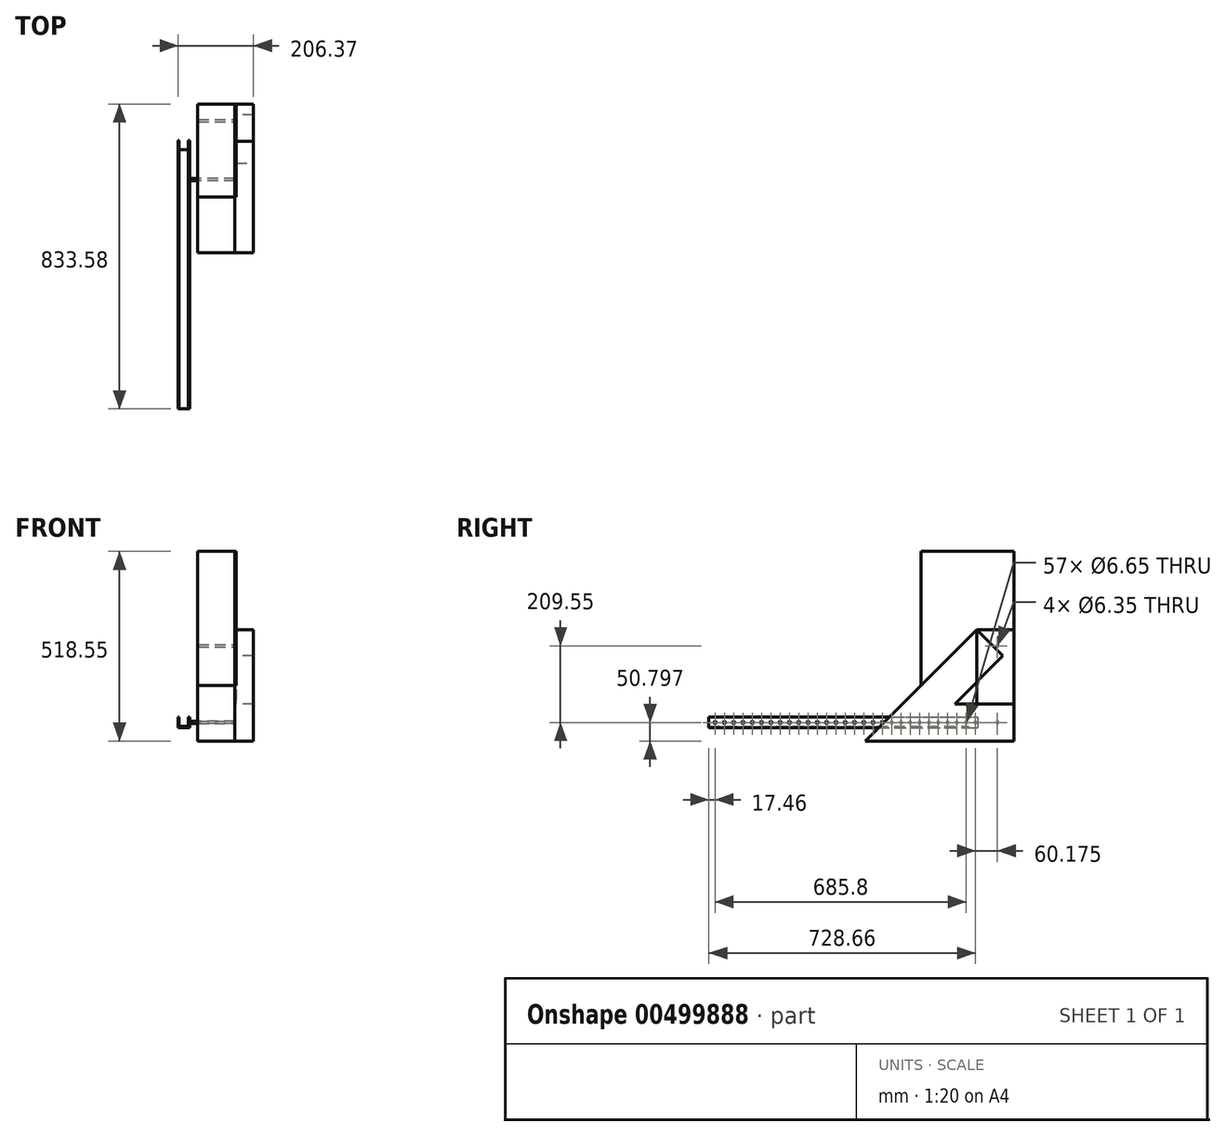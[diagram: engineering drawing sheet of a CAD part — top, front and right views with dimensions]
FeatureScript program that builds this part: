
annotation { "Feature Type Name" : "Feature", "Feature Type Description" : "" }
export const myFeature = defineFeature(function(context is Context, id is Id, definition is map)
    precondition{}
    {
        {
            var Q0;
            Q0=qCreatedBy(makeId("Front.planeOp"),FACE);
            var sketch = newSketch(context, id + "F0", { "sketchPlane" : qUnion([Q0])});
            skLineSegment(sketch, "E0", {"start": v(-56.5, 60.32) * mm, "end": v(-56.5, 31.75) * mm});
            skLineSegment(sketch, "E1", {"start": v(-56.5, 31.75) * mm, "end": v(-24.75, 31.75) * mm});
            skLineSegment(sketch, "E2", {"start": v(-24.75, 31.75) * mm, "end": v(-24.75, 60.33) * mm});
            skLineSegment(sketch, "E3", {"start": v(-24.75, 60.33) * mm, "end": v(-27.93, 60.33) * mm});
            skLineSegment(sketch, "E4", {"start": v(-27.93, 60.33) * mm, "end": v(-27.93, 34.92) * mm});
            skLineSegment(sketch, "E5", {"start": v(-27.93, 34.92) * mm, "end": v(-53.33, 34.92) * mm});
            skLineSegment(sketch, "E6", {"start": v(-53.33, 34.92) * mm, "end": v(-53.33, 60.32) * mm});
            skLineSegment(sketch, "E7", {"start": v(-53.33, 60.32) * mm, "end": v(-56.5, 60.32) * mm});
            skSolve(sketch);
        }
        {
            var Q0;
            Q0=qSketchRegion(id+"F0",true);
            extrude(context, id + "F1", {"entities" : qUnion([Q0]), "depth" : 735 * mm});
        }
        {
            var Q0;
            Q0=makeQuery(id+"F1.opExtrude","SWEPT_FACE",FACE,{"disambiguationData":[OSD([sQuery(id+"F0.wireOp",EDGE,"E2")])]});
            var sketch = newSketch(context, id + "F2", { "sketchPlane" : qUnion([Q0])});
            skLineSegment(sketch, "E8", {"start": v(-735.01, 46.04) * mm, "end": v(0, 46.04) * mm, "construction": true});
            skCircle(sketch, "E9", {"center": v(-6.35, 46.04) * mm, "radius": 3.18 * mm});
            skCircle(sketch, "E10", {"center": v(-31.75, 46.04) * mm, "radius": 3.32 * mm});
            skCircle(sketch, "E11.1.0.0", {"center": v(-57.15, 46.04) * mm, "radius": 3.32 * mm});
            skCircle(sketch, "E11.2.0.0", {"center": v(-82.55, 46.04) * mm, "radius": 3.32 * mm});
            skCircle(sketch, "E11.3.0.0", {"center": v(-107.95, 46.04) * mm, "radius": 3.32 * mm});
            skCircle(sketch, "E11.4.0.0", {"center": v(-133.35, 46.04) * mm, "radius": 3.32 * mm});
            skCircle(sketch, "E11.5.0.0", {"center": v(-158.75, 46.04) * mm, "radius": 3.32 * mm});
            skCircle(sketch, "E11.6.0.0", {"center": v(-184.15, 46.04) * mm, "radius": 3.32 * mm});
            skCircle(sketch, "E11.7.0.0", {"center": v(-209.55, 46.04) * mm, "radius": 3.32 * mm});
            skCircle(sketch, "E11.8.0.0", {"center": v(-234.95, 46.04) * mm, "radius": 3.32 * mm});
            skCircle(sketch, "E11.9.0.0", {"center": v(-260.35, 46.04) * mm, "radius": 3.32 * mm});
            skCircle(sketch, "E11.10.0.0", {"center": v(-285.75, 46.04) * mm, "radius": 3.32 * mm});
            skCircle(sketch, "E11.11.0.0", {"center": v(-311.15, 46.04) * mm, "radius": 3.32 * mm});
            skCircle(sketch, "E11.12.0.0", {"center": v(-336.55, 46.04) * mm, "radius": 3.32 * mm});
            skCircle(sketch, "E11.13.0.0", {"center": v(-361.95, 46.04) * mm, "radius": 3.32 * mm});
            skCircle(sketch, "E11.14.0.0", {"center": v(-387.35, 46.04) * mm, "radius": 3.32 * mm});
            skCircle(sketch, "E11.15.0.0", {"center": v(-412.75, 46.04) * mm, "radius": 3.32 * mm});
            skCircle(sketch, "E11.16.0.0", {"center": v(-438.15, 46.04) * mm, "radius": 3.32 * mm});
            skCircle(sketch, "E11.17.0.0", {"center": v(-463.55, 46.04) * mm, "radius": 3.32 * mm});
            skCircle(sketch, "E11.18.0.0", {"center": v(-488.95, 46.04) * mm, "radius": 3.32 * mm});
            skCircle(sketch, "E11.19.0.0", {"center": v(-514.35, 46.04) * mm, "radius": 3.32 * mm});
            skCircle(sketch, "E11.20.0.0", {"center": v(-539.75, 46.04) * mm, "radius": 3.32 * mm});
            skCircle(sketch, "E11.21.0.0", {"center": v(-565.15, 46.04) * mm, "radius": 3.32 * mm});
            skCircle(sketch, "E11.22.0.0", {"center": v(-590.55, 46.04) * mm, "radius": 3.32 * mm});
            skCircle(sketch, "E11.23.0.0", {"center": v(-615.95, 46.04) * mm, "radius": 3.32 * mm});
            skCircle(sketch, "E11.24.0.0", {"center": v(-641.35, 46.04) * mm, "radius": 3.32 * mm});
            skCircle(sketch, "E11.25.0.0", {"center": v(-666.75, 46.04) * mm, "radius": 3.32 * mm});
            skCircle(sketch, "E11.26.0.0", {"center": v(-692.15, 46.04) * mm, "radius": 3.32 * mm});
            skCircle(sketch, "E11.27.0.0", {"center": v(-717.55, 46.04) * mm, "radius": 3.32 * mm});
            skCircle(sketch, "E11.28.0.0", {"center": v(-742.95, 46.04) * mm, "radius": 3.32 * mm});
            skLineSegment(sketch, "E11.direction1", {"start": v(-31.75, 46.04) * mm, "end": v(-57.15, 46.04) * mm, "construction": true});
            skSolve(sketch);
        }
        {
            var Q0;
            Q0=qSketchRegion(id+"F2",true);
            var Q1;
            Q1=makeQuery(id+"F1.opExtrude","SWEPT_FACE",FACE,{"disambiguationData":[OSD([sQuery(id+"F0.wireOp",EDGE,"E0")])]});
            extrude(context, id + "F3", {"entities" : qUnion([Q0]), "operationType" : NewBodyOperationType.REMOVE, "endBound" : BoundingType.UP_TO_SURFACE, "oppositeDirection" : true, "endBoundEntityFace" : qUnion([Q1]), "depth" : 25.4 * mm});
        }
        {
            var Q0;
            Q0=makeQuery(id+"F1.opExtrude","SWEPT_FACE",FACE,{"disambiguationData":[OSD([sQuery(id+"F0.wireOp",EDGE,"E4")])]});
            var sketch = newSketch(context, id + "F4", { "sketchPlane" : qUnion([Q0])});
            skCircle(sketch, "E12.0", {"center": v(107.95, 46.04) * mm, "radius": 3.32 * mm});
            skSolve(sketch);
        }
        {
            var Q0;
            Q0=qSketchRegion(id+"F4",true);
            extrude(context, id + "F5", {"entities" : qUnion([Q0]), "oppositeDirection" : true, "depth" : 127 * mm});
        }
        {
            var Q0;
            Q0=makeQuery(id+"F5.opExtrude","CAP_FACE",FACE,{"disambiguationData":[OSD([sQuery(id+"F4.wireOp",EDGE,"E12.0")])],"isStart":false});
            var sketch = newSketch(context, id + "F6", { "sketchPlane" : qUnion([Q0])});
            skLineSegment(sketch, "E13.bottom", {"start": v(98.57, 0) * mm, "end": v(-155.43, 0) * mm});
            skLineSegment(sketch, "E13.top", {"start": v(98.57, 513.79) * mm, "end": v(-155.43, 513.79) * mm});
            skLineSegment(sketch, "E13.left", {"start": v(98.57, 0) * mm, "end": v(98.57, 513.79) * mm});
            skLineSegment(sketch, "E13.right", {"start": v(-155.43, 0) * mm, "end": v(-155.43, 513.79) * mm});
            skSolve(sketch);
        }
        {
            var Q0;
            Q0=qSketchRegion(id+"F6",true);
            extrude(context, id + "F7", {"entities" : qUnion([Q0]), "operationType" : NewBodyOperationType.ADD, "depth" : 3.17 * mm});
        }
        {
            var Q0;
            Q0=makeQuery(id+"F1.opExtrude","SWEPT_FACE",FACE,{"disambiguationData":[OSD([sQuery(id+"F0.wireOp",EDGE,"E1")])]});
            var sketch = newSketch(context, id + "F8", { "sketchPlane" : qUnion([Q0])});
            skLineSegment(sketch, "E14.0", {"start": v(-53.33, 735.01) * mm, "end": v(-53.33, 0) * mm});
            skLineSegment(sketch, "E15.0", {"start": v(-27.93, 735.01) * mm, "end": v(-27.93, 0) * mm});
            skLineSegment(sketch, "E16", {"start": v(-53.33, 0) * mm, "end": v(-27.93, 0) * mm});
            skLineSegment(sketch, "E17", {"start": v(-53.33, 25.4) * mm, "end": v(-27.93, 25.4) * mm});
            skSolve(sketch);
        }
        {
            var Q0;
            Q0=qSketchRegion(id+"F8",true);
            extrude(context, id + "F9", {"entities" : qUnion([Q0]), "operationType" : NewBodyOperationType.REMOVE, "oppositeDirection" : true, "depth" : 25.4 * mm});
        }
        {
            var Q0;
            Q0=makeQuery(id+"F7.opExtrude","CAP_FACE",FACE,{"disambiguationData":[OSD([sQuery(id+"F6.wireOp",EDGE,"E13.bottom"),sQuery(id+"F6.wireOp",EDGE,"E13.top"),sQuery(id+"F6.wireOp",EDGE,"E13.left"),sQuery(id+"F6.wireOp",EDGE,"E13.right")])],"isStart":true});
            var sketch = newSketch(context, id + "F10", { "sketchPlane" : qUnion([Q0])});
            skLineSegment(sketch, "E18", {"start": v(107.95, 46.04) * mm, "end": v(-98.57, 46.04) * mm, "construction": true});
            skLineSegment(sketch, "E19", {"start": v(-98.57, -4.76) * mm, "end": v(155.43, -4.76) * mm});
            skLineSegment(sketch, "E20", {"start": v(155.43, -4.76) * mm, "end": v(155.43, 96.84) * mm});
            skLineSegment(sketch, "E21", {"start": v(155.43, 96.84) * mm, "end": v(-98.57, 96.84) * mm});
            skLineSegment(sketch, "E22", {"start": v(-98.57, 96.84) * mm, "end": v(-98.57, -4.76) * mm});
            skSolve(sketch);
        }
        {
            var Q0;
            Q0=qSketchRegion(id+"F10",true);
            extrude(context, id + "F11", {"entities" : qUnion([Q0]), "oppositeDirection" : true, "depth" : 50.8 * mm});
        }
        {
            var Q0;
            Q0=makeQuery(id+"F11.opExtrude","SWEPT_FACE",FACE,{"disambiguationData":[OSD([sQuery(id+"F10.wireOp",EDGE,"E21")])]});
            var sketch = newSketch(context, id + "F12", { "sketchPlane" : qUnion([Q0])});
            skLineSegment(sketch, "E23.0.0", {"start": v(99.07, 98.57) * mm, "end": v(99.07, -155.43) * mm});
            skLineSegment(sketch, "E23.0.1", {"start": v(99.07, -155.43) * mm, "end": v(149.87, -155.43) * mm});
            skLineSegment(sketch, "E23.0.2", {"start": v(149.87, -155.43) * mm, "end": v(149.87, 98.57) * mm});
            skLineSegment(sketch, "E23.0.3", {"start": v(149.87, 98.57) * mm, "end": v(99.07, 98.57) * mm});
            skLineSegment(sketch, "E24", {"start": v(149.87, -3.03) * mm, "end": v(99.07, -3.03) * mm});
            skSolve(sketch);
        }
        {
            var Q0;
            {var subQ0=sQuery(id+"F12.wireOp",EDGE,"E23.0.3");Q0=makeQuery(id+"F12.imprint","IMPRINT",FACE,{"disambiguationData":[TD([[makeQuery(id+"F12.imprint","IMPRINT",EDGE,{"derivedFrom":subQ0}),1.0]])]});}
            extrude(context, id + "F13", {"entities" : qUnion([Q0]), "depth" : 203.2 * mm});
        }
        {
            var Q0;
            Q0=makeQuery(id+"F7.opExtrude","CAP_FACE",FACE,{"disambiguationData":[OSD([sQuery(id+"F6.wireOp",EDGE,"E13.bottom"),sQuery(id+"F6.wireOp",EDGE,"E13.top"),sQuery(id+"F6.wireOp",EDGE,"E13.left"),sQuery(id+"F6.wireOp",EDGE,"E13.right")])],"isStart":true});
            var sketch = newSketch(context, id + "F14", { "sketchPlane" : qUnion([Q0])});
            skCircle(sketch, "E25.0", {"center": v(-53.83, 46.04) * mm, "radius": 3.18 * mm});
            skLineSegment(sketch, "E26", {"start": v(-53.83, 46.04) * mm, "end": v(-53.83, 255.59) * mm, "construction": true});
            skCircle(sketch, "E27", {"center": v(-53.83, 255.59) * mm, "radius": 3.18 * mm});
            skSolve(sketch);
        }
        {
            var Q0;
            Q0=makeQuery(id+"F13.opExtrude","SWEPT_BODY",BODY,{"disambiguationData":[OSD([sQuery(id+"F12.wireOp",EDGE,"E23.0.0"),sQuery(id+"F12.wireOp",EDGE,"E23.0.2"),sQuery(id+"F12.wireOp",EDGE,"E23.0.3"),sQuery(id+"F12.wireOp",EDGE,"E24")])]});
            var Q1;
            Q1=makeQuery(id+"F13.opExtrude","CAP_EDGE",EDGE,{"disambiguationData":[OSD([sQuery(id+"F12.wireOp",EDGE,"E24")])],"isStart":false});
            transform(context, id + "F15", {"entities" : qUnion([Q0]), "transformType" : TransformType.ROTATION, "transformAxis" : qUnion([Q1]), "angle" : 45 * degree, "makeCopy" : true});
        }
        {
            var Q0;
            Q0=makeQuery(id+"F15.opPattern","COPY",FACE,{"derivedFrom":makeQuery(id+"F13.opExtrude","CAP_FACE",FACE,{"disambiguationData":[OSD([sQuery(id+"F12.wireOp",EDGE,"E23.0.0"),sQuery(id+"F12.wireOp",EDGE,"E23.0.2"),sQuery(id+"F12.wireOp",EDGE,"E23.0.3"),sQuery(id+"F12.wireOp",EDGE,"E24")])],"isStart":true}),"instanceName":"1"});
            var Q1;
            Q1=makeQuery(id+"F11.opExtrude","SWEPT_FACE",FACE,{"disambiguationData":[OSD([sQuery(id+"F10.wireOp",EDGE,"E21")])]});
            extrude(context, id + "F16", {"entities" : qUnion([Q0]), "operationType" : NewBodyOperationType.ADD, "endBound" : BoundingType.UP_TO_SURFACE, "endBoundEntityFace" : qUnion([Q1]), "depth" : 25.4 * mm});
        }
        {
            var Q0;
            Q0=makeQuery(id+"F11.opExtrude","SWEPT_FACE",FACE,{"disambiguationData":[OSD([sQuery(id+"F10.wireOp",EDGE,"E20")])]});
            var sketch = newSketch(context, id + "F17", { "sketchPlane" : qUnion([Q0])});
            skLineSegment(sketch, "E28.0.0", {"start": v(99.07, 96.84) * mm, "end": v(99.07, -4.76) * mm});
            skLineSegment(sketch, "E28.0.1", {"start": v(99.07, -4.76) * mm, "end": v(149.87, -4.76) * mm});
            skLineSegment(sketch, "E28.0.2", {"start": v(149.87, -4.76) * mm, "end": v(149.87, 96.84) * mm});
            skLineSegment(sketch, "E28.0.3", {"start": v(149.87, 96.84) * mm, "end": v(99.07, 96.84) * mm});
            skSolve(sketch);
        }
        {
            var Q0;
            Q0=qSketchRegion(id+"F17",true);
            var Q1;
            {var subQ0=sQuery(id+"F12.wireOp",EDGE,"E24");Q1=makeQuery(id+"F16.boolean.opBoolean","MERGE",FACE,{"derivedFrom":[makeQuery(id+"F15.opPattern","COPY",FACE,{"derivedFrom":makeQuery(id+"F13.opExtrude","SWEPT_FACE",FACE,{"disambiguationData":[OSD([subQ0])]}),"instanceName":"1"}),makeQuery(id+"F16.opExtrude","SWEPT_FACE",FACE,{"disambiguationData":[OSD([subQ0])]})]});}
            extrude(context, id + "F18", {"entities" : qUnion([Q0]), "operationType" : NewBodyOperationType.ADD, "endBound" : BoundingType.UP_TO_SURFACE, "endBoundEntityFace" : qUnion([Q1]), "depth" : 25.4 * mm});
        }
        {
            var Q0;
            Q0=makeQuery(id+"F18.boolean.opBoolean","MERGE",FACE,{"derivedFrom":[makeQuery(id+"F11.opExtrude","CAP_FACE",FACE,{"disambiguationData":[OSD([sQuery(id+"F10.wireOp",EDGE,"E19"),sQuery(id+"F10.wireOp",EDGE,"E20"),sQuery(id+"F10.wireOp",EDGE,"E21"),sQuery(id+"F10.wireOp",EDGE,"E22")])],"isStart":true}),makeQuery(id+"F18.opExtrude","SWEPT_FACE",FACE,{"disambiguationData":[OSD([sQuery(id+"F17.wireOp",EDGE,"E28.0.0")])]})]});
            var sketch = newSketch(context, id + "F19", { "sketchPlane" : qUnion([Q0])});
            skCircle(sketch, "E29.0", {"center": v(107.95, 46.04) * mm, "radius": 3.32 * mm});
            skCircle(sketch, "E30.0", {"center": v(-53.83, 46.04) * mm, "radius": 3.18 * mm});
            skCircle(sketch, "E31.0", {"center": v(-53.83, 255.59) * mm, "radius": 3.18 * mm});
            skSolve(sketch);
        }
        {
            var Q0;
            Q0=makeQuery(id+"F14.imprint","IMPRINT",FACE,{"disambiguationData":[TD([[makeQuery(id+"F14.imprint","IMPRINT",EDGE,{"derivedFrom":sQuery(id+"F14.wireOp",EDGE,"E27")}),1.0]])]});
            extrude(context, id + "F20", {"entities" : qUnion([Q0]), "depth" : 101.6 * mm});
        }
        {
            var Q0;
            Q0=makeQuery(id+"F19.imprint","IMPRINT",FACE,{"disambiguationData":[TD([[makeQuery(id+"F19.imprint","IMPRINT",EDGE,{"derivedFrom":sQuery(id+"F19.wireOp",EDGE,"E29.0")}),1.0]])]});
            extrude(context, id + "F21", {"entities" : qUnion([Q0]), "depth" : 101.6 * mm});
        }
    });
